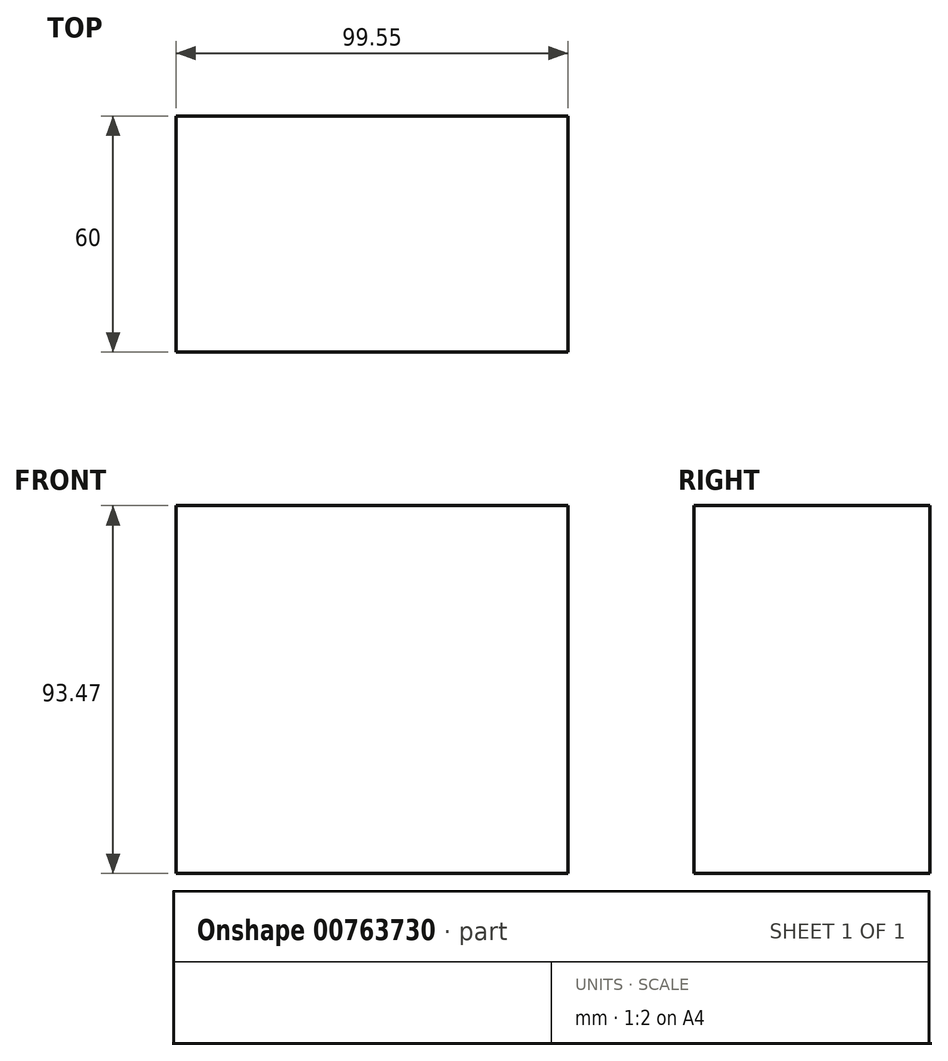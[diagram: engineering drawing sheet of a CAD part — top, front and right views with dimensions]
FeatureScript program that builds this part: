
annotation { "Feature Type Name" : "Feature", "Feature Type Description" : "" }
export const myFeature = defineFeature(function(context is Context, id is Id, definition is map)
    precondition{}
    {
        {
            var Q0;
            Q0=qCreatedBy(makeId("Front.planeOp"),FACE);
            var sketch = newSketch(context, id + "F0", { "sketchPlane" : qUnion([Q0])});
            skLineSegment(sketch, "E0.bottom", {"start": v(0, 0) * mm, "end": v(-300, 0) * mm, "construction": true});
            skLineSegment(sketch, "E0.top", {"start": v(0, -200) * mm, "end": v(-300, -200) * mm, "construction": true});
            skLineSegment(sketch, "E0.left", {"start": v(0, 0) * mm, "end": v(0, -200) * mm, "construction": true});
            skLineSegment(sketch, "E0.right", {"start": v(-300, 0) * mm, "end": v(-300, -200) * mm, "construction": true});
            skLineSegment(sketch, "E1.bottom", {"start": v(-186.61, -42.15) * mm, "end": v(-87.06, -42.15) * mm});
            skLineSegment(sketch, "E1.top", {"start": v(-186.61, -135.62) * mm, "end": v(-87.06, -135.62) * mm});
            skLineSegment(sketch, "E1.left", {"start": v(-186.61, -42.15) * mm, "end": v(-186.61, -135.62) * mm});
            skLineSegment(sketch, "E1.right", {"start": v(-87.06, -42.15) * mm, "end": v(-87.06, -135.62) * mm});
            skSolve(sketch);
        }
        {
            var Q0;
            Q0 = qSketchRegion(id + "F0", true);
            extrude(context, id + "F1", {"entities" : qUnion([Q0]), "depth" : 60 * mm, "offsetDistance" : 25 * mm});
        }
    });
